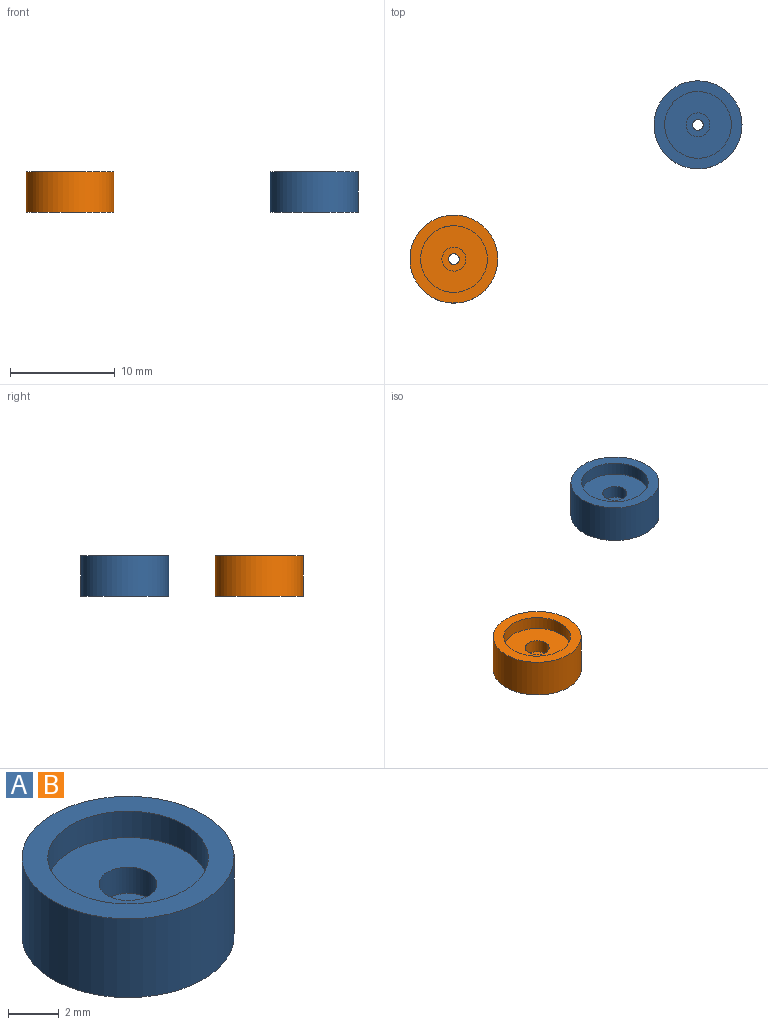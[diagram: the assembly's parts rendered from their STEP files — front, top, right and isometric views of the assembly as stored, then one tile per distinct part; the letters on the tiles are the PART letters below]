
ASSEMBLY  parts=2 mates=1
PART A: 8 faces, bbox 8.4x8.4x3.8 mm
  f0: plane 2.29x2.29mm, normal (0,0,1), area 3.3mm2, adj f1,f7
  f1: cylinder r=1.14mm len=2.29mm, axis (0,0,1), area 9.1mm2, adj f0,f2
  f2: plane 6.35x6.35mm, normal (0,0,1), area 27.6mm2, adj f1,f3
  f3: cylinder r=3.17mm len=6.35mm, axis (0,0,1), area 25.3mm2, adj f2,f4
  f4: plane 8.38x8.38mm, normal (0,0,1), area 23.5mm2, adj f3,f5
  f5: cylinder r=4.19mm len=8.38mm, axis (0,0,1), area 100.3mm2, adj f4,f6
  f6: plane 8.38x8.38mm, normal (0,0,-1), area 54.4mm2, adj f5,f7
  f7: cylinder r=0.51mm len=1.27mm, axis (0,0,1), area 4.1mm2, adj f0,f6
PART B: same geometry as A
PLACE A t=(-5.43,-3.12,1.37)mm
PLACE B t=(-28.68,-15.9,1.37)mm fixed
MATE planar A.f1 <-> B.f1  axis (0,0,-1) through (-5.43,-3.12,-1.17)mm
